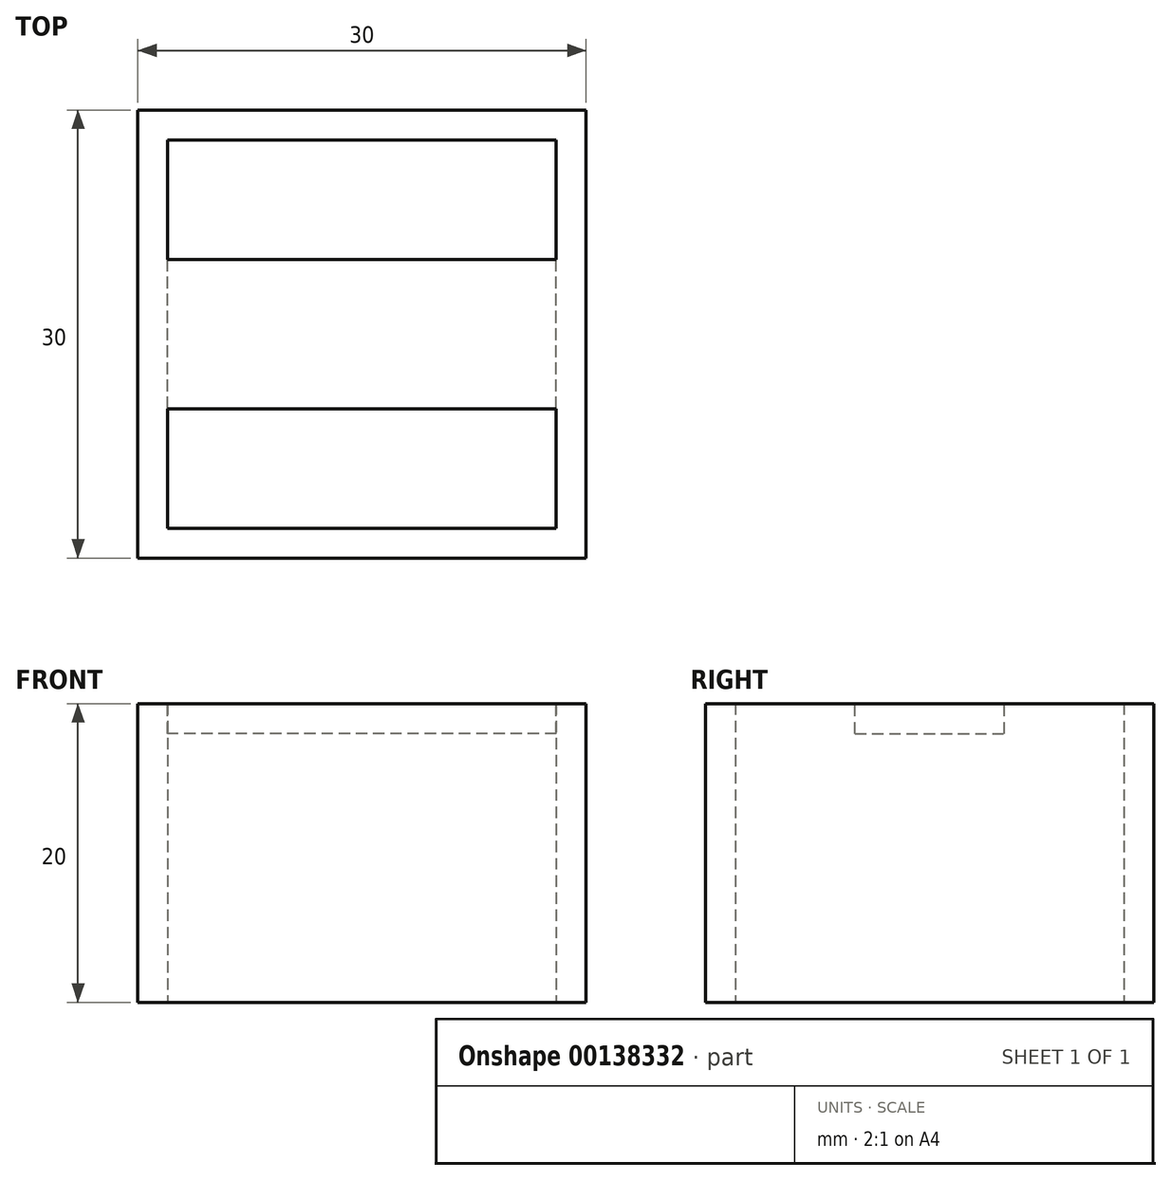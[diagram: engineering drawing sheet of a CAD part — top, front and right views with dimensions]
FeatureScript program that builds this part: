
annotation { "Feature Type Name" : "Feature", "Feature Type Description" : "" }
export const myFeature = defineFeature(function(context is Context, id is Id, definition is map)
    precondition{}
    {
        {
            var Q0;
            Q0=qCreatedBy(makeId("Top.planeOp"),FACE);
            var sketch = newSketch(context, id + "F0", { "sketchPlane" : qUnion([Q0])});
            skLineSegment(sketch, "E0.bottom", {"start": v(15, -15) * mm, "end": v(-15, -15) * mm});
            skLineSegment(sketch, "E0.top", {"start": v(15, 15) * mm, "end": v(-15, 15) * mm});
            skLineSegment(sketch, "E0.left", {"start": v(15, -15) * mm, "end": v(15, 15) * mm});
            skLineSegment(sketch, "E0.right", {"start": v(-15, -15) * mm, "end": v(-15, 15) * mm});
            skPoint(sketch, "E0.middle", {"position": v(0, 0) * mm});
            skLineSegment(sketch, "E1.0", {"start": v(13, 13) * mm, "end": v(-13, 13) * mm});
            skLineSegment(sketch, "E1.1", {"start": v(13, -13) * mm, "end": v(13, 13) * mm});
            skLineSegment(sketch, "E1.2", {"start": v(13, -13) * mm, "end": v(-13, -13) * mm});
            skLineSegment(sketch, "E1.3", {"start": v(-13, -13) * mm, "end": v(-13, 13) * mm});
            skSolve(sketch);
        }
        {
            var Q0;
            Q0=makeQuery(id+"F0.imprint","IMPRINT",FACE,{"disambiguationData":[TD([[makeQuery(id+"F0.imprint","IMPRINT",EDGE,{"derivedFrom":sQuery(id+"F0.wireOp",EDGE,"E0.bottom")}),-1.0]])]});
            extrude(context, id + "F1", {"entities" : qUnion([Q0]), "depth" : 20 * mm});
        }
        {
            var Q0;
            Q0=makeQuery(id+"F1.opExtrude","CAP_FACE",FACE,{"disambiguationData":[OSD([sQuery(id+"F0.wireOp",EDGE,"E0.bottom"),sQuery(id+"F0.wireOp",EDGE,"E0.top"),sQuery(id+"F0.wireOp",EDGE,"E0.left"),sQuery(id+"F0.wireOp",EDGE,"E0.right"),sQuery(id+"F0.wireOp",EDGE,"E1.0"),sQuery(id+"F0.wireOp",EDGE,"E1.1"),sQuery(id+"F0.wireOp",EDGE,"E1.2"),sQuery(id+"F0.wireOp",EDGE,"E1.3")])],"isStart":false});
            var sketch = newSketch(context, id + "F2", { "sketchPlane" : qUnion([Q0])});
            skLineSegment(sketch, "E2.bottom", {"start": v(13, -5) * mm, "end": v(-13, -5) * mm});
            skLineSegment(sketch, "E2.top", {"start": v(13, 5) * mm, "end": v(-13, 5) * mm});
            skLineSegment(sketch, "E2.left", {"start": v(13, -5) * mm, "end": v(13, 5) * mm});
            skLineSegment(sketch, "E2.right", {"start": v(-13, -5) * mm, "end": v(-13, 5) * mm});
            skPoint(sketch, "E2.middle", {"position": v(0, 0) * mm});
            skSolve(sketch);
        }
        {
            var Q0;
            Q0=makeQuery(id+"F2.imprint","IMPRINT",FACE,{"disambiguationData":[TD([[makeQuery(id+"F2.imprint","IMPRINT",EDGE,{"derivedFrom":sQuery(id+"F2.wireOp",EDGE,"E2.bottom")}),-1.0]])]});
            extrude(context, id + "F3", {"entities" : qUnion([Q0]), "operationType" : NewBodyOperationType.ADD, "oppositeDirection" : true, "depth" : 2 * mm});
        }
    });
